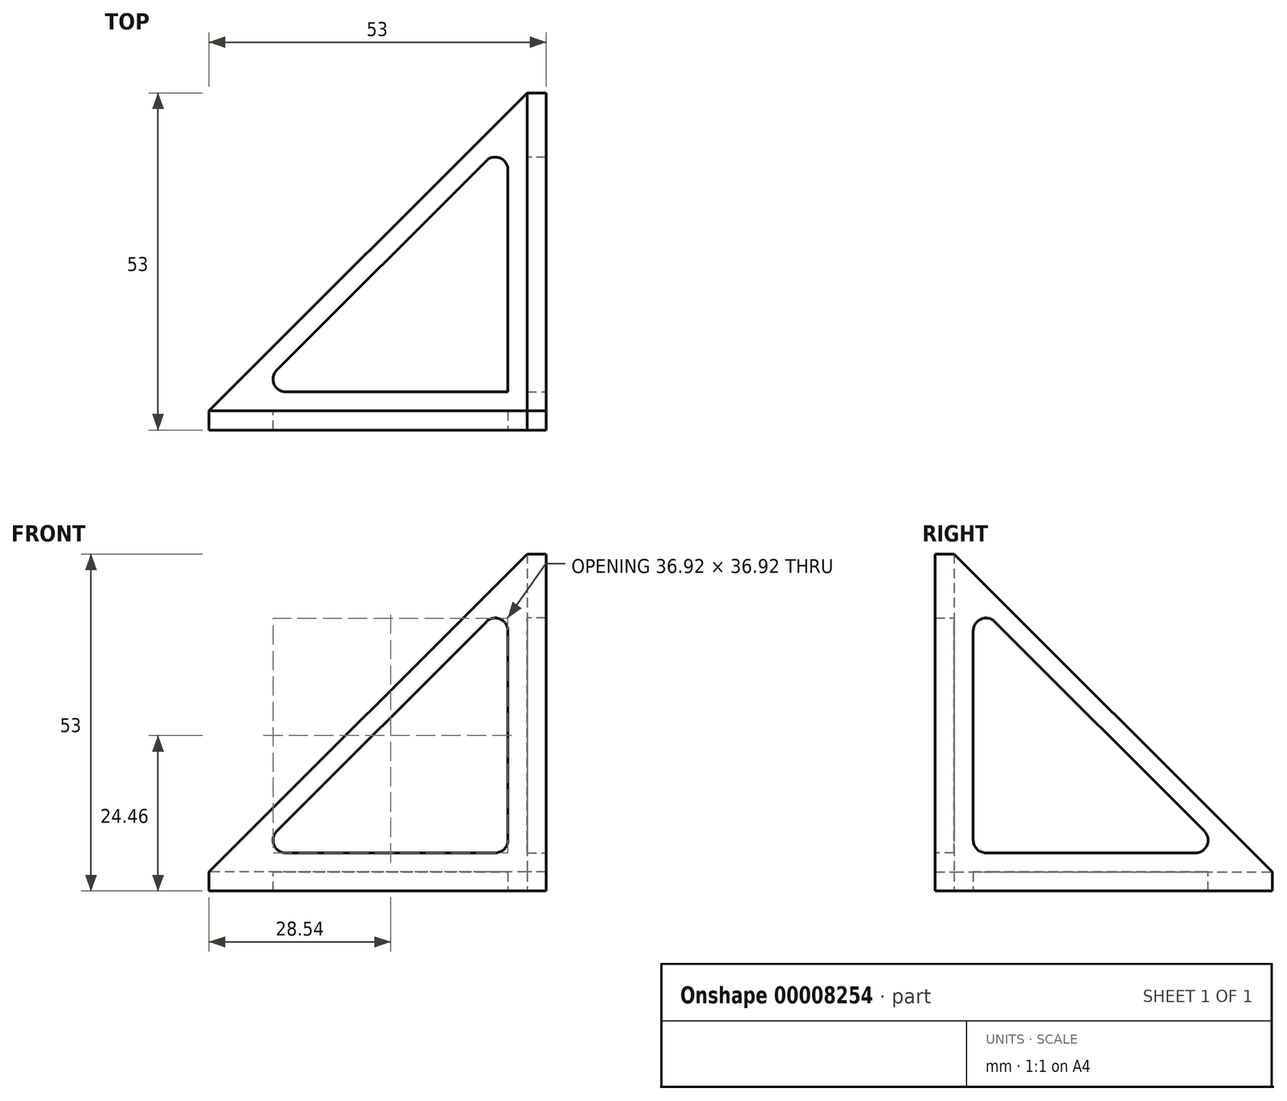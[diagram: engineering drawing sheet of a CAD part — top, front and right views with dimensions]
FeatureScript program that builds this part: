
annotation { "Feature Type Name" : "Feature", "Feature Type Description" : "" }
export const myFeature = defineFeature(function(context is Context, id is Id, definition is map)
    precondition{}
    {
        {
            var Q0;
            Q0=qCreatedBy(makeId("Top.planeOp"),FACE);
            var sketch = newSketch(context, id + "F0", { "sketchPlane" : qUnion([Q0])});
            skLineSegment(sketch, "E0", {"start": v(-3, 0) * mm, "end": v(-53, 0) * mm});
            skLineSegment(sketch, "E1", {"start": v(-53, 0) * mm, "end": v(-53, 3) * mm});
            skLineSegment(sketch, "E2", {"start": v(-53, 3) * mm, "end": v(-3, 3) * mm});
            skLineSegment(sketch, "E3", {"start": v(0, 3) * mm, "end": v(0, 53) * mm});
            skLineSegment(sketch, "E4", {"start": v(0, 53) * mm, "end": v(-3, 53) * mm});
            skLineSegment(sketch, "E5", {"start": v(-3, 53) * mm, "end": v(-3, 3) * mm});
            skLineSegment(sketch, "E6", {"start": v(-3, 0) * mm, "end": v(0, 0) * mm});
            skLineSegment(sketch, "E7", {"start": v(-3, 3) * mm, "end": v(0, 3) * mm});
            skLineSegment(sketch, "E8", {"start": v(0, 3) * mm, "end": v(0, 0) * mm});
            skLineSegment(sketch, "E9", {"start": v(-3, 3) * mm, "end": v(-3, 0) * mm});
            skLineSegment(sketch, "E10", {"start": v(-53, 3) * mm, "end": v(-3, 53) * mm});
            skLineSegment(sketch, "E11", {"start": v(-45.76, 6) * mm, "end": v(-6, 6) * mm});
            skLineSegment(sketch, "E12", {"start": v(-6, 6) * mm, "end": v(-6, 45.76) * mm});
            skLineSegment(sketch, "E13", {"start": v(-6, 45.76) * mm, "end": v(-45.76, 6) * mm});
            skLineSegment(sketch, "E14", {"start": v(-6, 25.88) * mm, "end": v(-3, 25.88) * mm, "construction": true});
            skLineSegment(sketch, "E15", {"start": v(-25.88, 6) * mm, "end": v(-25.88, 3) * mm, "construction": true});
            skLineSegment(sketch, "E16", {"start": v(-25.88, 25.88) * mm, "end": v(-28, 28) * mm, "construction": true});
            skSolve(sketch);
        }
        {
            var Q0;
            Q0=makeQuery(id+"F0.imprint","IMPRINT",FACE,{"disambiguationData":[TD([[makeQuery(id+"F0.imprint","IMPRINT",EDGE,{"derivedFrom":sQuery(id+"F0.wireOp",EDGE,"E2")}),1.0]])]});
            var Q1;
            Q1=makeQuery(id+"F0.imprint","IMPRINT",FACE,{"disambiguationData":[TD([[makeQuery(id+"F0.imprint","IMPRINT",EDGE,{"derivedFrom":sQuery(id+"F0.wireOp",EDGE,"E0")}),-1.0]])]});
            var Q2;
            Q2=makeQuery(id+"F0.imprint","IMPRINT",FACE,{"disambiguationData":[TD([[makeQuery(id+"F0.imprint","IMPRINT",EDGE,{"derivedFrom":sQuery(id+"F0.wireOp",EDGE,"E6")}),1.0]])]});
            var Q3;
            Q3=makeQuery(id+"F0.imprint","IMPRINT",FACE,{"disambiguationData":[TD([[makeQuery(id+"F0.imprint","IMPRINT",EDGE,{"derivedFrom":sQuery(id+"F0.wireOp",EDGE,"E3")}),1.0]])]});
            extrude(context, id + "F1", {"entities" : qUnion([Q0, Q1, Q2, Q3]), "depth" : 3 * mm});
        }
        {
            var Q0;
            Q0=qCreatedBy(makeId("Right.planeOp"),FACE);
            var sketch = newSketch(context, id + "F2", { "sketchPlane" : qUnion([Q0])});
            skLineSegment(sketch, "E17.0.0", {"start": v(3, 0) * mm, "end": v(53, 0) * mm});
            skLineSegment(sketch, "E17.0.1", {"start": v(53, 0) * mm, "end": v(53, 3) * mm});
            skLineSegment(sketch, "E17.0.2", {"start": v(53, 3) * mm, "end": v(3, 3) * mm});
            skLineSegment(sketch, "E18", {"start": v(0, 3) * mm, "end": v(0, 53) * mm});
            skLineSegment(sketch, "E19", {"start": v(0, 53) * mm, "end": v(3, 53) * mm});
            skLineSegment(sketch, "E20", {"start": v(3, 53) * mm, "end": v(3, 3) * mm});
            skPoint(sketch, "E21", {"position": v(3, 3) * mm});
            skLineSegment(sketch, "E22", {"start": v(3, 3) * mm, "end": v(3, 0) * mm});
            skPoint(sketch, "E17.0.3.end.orphan", {"position": v(0, 0) * mm});
            skLineSegment(sketch, "E23", {"start": v(0, 3) * mm, "end": v(3, 3) * mm});
            skLineSegment(sketch, "E24", {"start": v(0, 3) * mm, "end": v(0, 0) * mm});
            skLineSegment(sketch, "E25", {"start": v(0, 0) * mm, "end": v(3, 0) * mm});
            skLineSegment(sketch, "E26", {"start": v(3, 53) * mm, "end": v(53, 3) * mm});
            skLineSegment(sketch, "E27", {"start": v(6, 6) * mm, "end": v(6, 45.76) * mm});
            skLineSegment(sketch, "E28", {"start": v(6, 45.76) * mm, "end": v(45.76, 6) * mm});
            skLineSegment(sketch, "E29", {"start": v(45.76, 6) * mm, "end": v(6, 6) * mm});
            skPoint(sketch, "E30", {"position": v(6, 25.88) * mm});
            skPoint(sketch, "E31", {"position": v(25.88, 25.88) * mm});
            skPoint(sketch, "E32", {"position": v(25.88, 6) * mm});
            skLineSegment(sketch, "E33", {"start": v(6, 25.88) * mm, "end": v(3, 25.88) * mm, "construction": true});
            skLineSegment(sketch, "E34", {"start": v(25.88, 25.88) * mm, "end": v(28, 28) * mm, "construction": true});
            skLineSegment(sketch, "E35", {"start": v(25.88, 6) * mm, "end": v(25.88, 3) * mm, "construction": true});
            skSolve(sketch);
        }
        {
            var Q0;
            Q0=makeQuery(id+"F2.imprint","IMPRINT",FACE,{"disambiguationData":[TD([[makeQuery(id+"F2.imprint","IMPRINT",EDGE,{"derivedFrom":sQuery(id+"F2.wireOp",EDGE,"E18")}),-1.0]])]});
            var Q1;
            Q1=makeQuery(id+"F2.imprint","IMPRINT",FACE,{"disambiguationData":[TD([[makeQuery(id+"F2.imprint","IMPRINT",EDGE,{"derivedFrom":sQuery(id+"F2.wireOp",EDGE,"E17.0.2")}),-1.0]])]});
            extrude(context, id + "F3", {"entities" : qUnion([Q0, Q1]), "operationType" : NewBodyOperationType.ADD, "oppositeDirection" : true, "depth" : 3 * mm});
        }
        {
            var Q0;
            Q0=qCreatedBy(makeId("Front.planeOp"),FACE);
            var sketch = newSketch(context, id + "F4", { "sketchPlane" : qUnion([Q0])});
            skLineSegment(sketch, "E36.0.0", {"start": v(-53, 0) * mm, "end": v(0, 0) * mm});
            skLineSegment(sketch, "E36.0.1", {"start": v(0, 0) * mm, "end": v(0, 53) * mm});
            skLineSegment(sketch, "E36.0.2", {"start": v(0, 53) * mm, "end": v(-3, 53) * mm});
            skLineSegment(sketch, "E36.0.3", {"start": v(-3, 53) * mm, "end": v(-3, 3) * mm});
            skLineSegment(sketch, "E36.0.4", {"start": v(-3, 3) * mm, "end": v(-53, 3) * mm});
            skLineSegment(sketch, "E36.0.5", {"start": v(-53, 3) * mm, "end": v(-53, 0) * mm});
            skLineSegment(sketch, "E37", {"start": v(-53, 3) * mm, "end": v(-3, 53) * mm});
            skLineSegment(sketch, "E38", {"start": v(-6, 6) * mm, "end": v(-6, 45.76) * mm});
            skLineSegment(sketch, "E39", {"start": v(-6, 45.76) * mm, "end": v(-45.76, 6) * mm});
            skLineSegment(sketch, "E40", {"start": v(-45.76, 6) * mm, "end": v(-6, 6) * mm});
            skPoint(sketch, "E41", {"position": v(-25.88, 6) * mm});
            skPoint(sketch, "E42", {"position": v(-6, 25.88) * mm});
            skPoint(sketch, "E43", {"position": v(-25.88, 25.88) * mm});
            skLineSegment(sketch, "E44", {"start": v(-25.88, 25.88) * mm, "end": v(-28, 28) * mm, "construction": true});
            skLineSegment(sketch, "E45", {"start": v(-25.88, 6) * mm, "end": v(-25.88, 3) * mm, "construction": true});
            skLineSegment(sketch, "E46", {"start": v(-6, 25.88) * mm, "end": v(-3, 25.88) * mm, "construction": true});
            skLineSegment(sketch, "E47", {"start": v(-3, 3) * mm, "end": v(-3, 0) * mm, "construction": true});
            skSolve(sketch);
        }
        {
            var Q0;
            Q0=makeQuery(id+"F4.imprint","IMPRINT",FACE,{"disambiguationData":[TD([[makeQuery(id+"F4.imprint","IMPRINT",EDGE,{"derivedFrom":sQuery(id+"F4.wireOp",EDGE,"E36.0.3")}),-1.0]])]});
            extrude(context, id + "F5", {"entities" : qUnion([Q0]), "operationType" : NewBodyOperationType.ADD, "oppositeDirection" : true, "depth" : 3 * mm});
        }
        {
            var Q0;
            Q0=makeQuery(id+"F5.opExtrude","CAP_EDGE",EDGE,{"disambiguationData":[OSD([sQuery(id+"F4.wireOp",EDGE,"E36.0.3")])],"isStart":false});
            var Q1;
            Q1=makeQuery(id+"F5.opExtrude","CAP_EDGE",EDGE,{"disambiguationData":[OSD([sQuery(id+"F4.wireOp",EDGE,"E36.0.4")])],"isStart":false});
            var Q2;
            Q2=makeQuery(id+"F3.opExtrude","CAP_EDGE",EDGE,{"disambiguationData":[OSD([sQuery(id+"F2.wireOp",EDGE,"E17.0.2"),sQuery(id+"F2.wireOp",EDGE,"E23")])],"isStart":false});
            var Q3;
            Q3=makeQuery(id+"F3.opExtrude","SWEPT_EDGE",EDGE,{"disambiguationData":[OSD([sQuery(id+"F2.wireOp",EDGE,"E27"),sQuery(id+"F2.wireOp",EDGE,"E29")])]});
            var Q4;
            Q4=makeQuery(id+"F5.opExtrude","SWEPT_EDGE",EDGE,{"disambiguationData":[OSD([sQuery(id+"F4.wireOp",EDGE,"E38"),sQuery(id+"F4.wireOp",EDGE,"E40")])]});
            var Q5;
            Q5=makeQuery(id+"F3.opExtrude","SWEPT_EDGE",EDGE,{"disambiguationData":[OSD([sQuery(id+"F2.wireOp",EDGE,"E28"),sQuery(id+"F2.wireOp",EDGE,"E29")])]});
            var Q6;
            Q6=makeQuery(id+"F1.opExtrude","SWEPT_EDGE",EDGE,{"disambiguationData":[OSD([sQuery(id+"F0.wireOp",EDGE,"E12"),sQuery(id+"F0.wireOp",EDGE,"E13")])]});
            var Q7;
            Q7=makeQuery(id+"F5.opExtrude","SWEPT_EDGE",EDGE,{"disambiguationData":[OSD([sQuery(id+"F4.wireOp",EDGE,"E38"),sQuery(id+"F4.wireOp",EDGE,"E39")])]});
            var Q8;
            Q8=makeQuery(id+"F3.opExtrude","SWEPT_EDGE",EDGE,{"disambiguationData":[OSD([sQuery(id+"F2.wireOp",EDGE,"E27"),sQuery(id+"F2.wireOp",EDGE,"E28")])]});
            var Q9;
            Q9=makeQuery(id+"F5.opExtrude","SWEPT_EDGE",EDGE,{"disambiguationData":[OSD([sQuery(id+"F4.wireOp",EDGE,"E39"),sQuery(id+"F4.wireOp",EDGE,"E40")])]});
            var Q10;
            Q10=makeQuery(id+"F1.opExtrude","SWEPT_EDGE",EDGE,{"disambiguationData":[OSD([sQuery(id+"F0.wireOp",EDGE,"E11"),sQuery(id+"F0.wireOp",EDGE,"E13")])]});
            fillet(context, id + "F6", {"entities" : qUnion([Q0, Q1, Q2, Q3, Q4, Q5, Q6, Q7, Q8, Q9, Q10]), "radius" : 2 * mm, "tangentPropagation" : true, "allowEdgeOverflow" : false});
        }
    });
